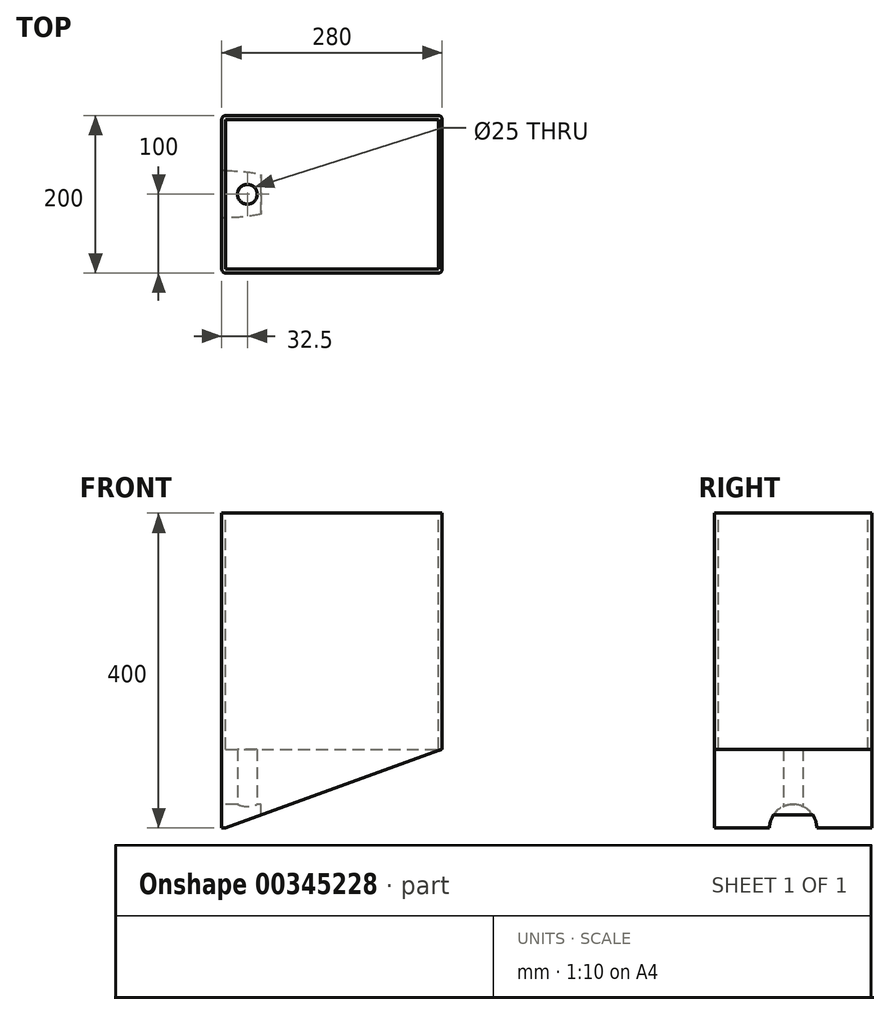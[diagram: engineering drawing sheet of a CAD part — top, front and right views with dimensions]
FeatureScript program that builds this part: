
annotation { "Feature Type Name" : "Feature", "Feature Type Description" : "" }
export const myFeature = defineFeature(function(context is Context, id is Id, definition is map)
    precondition{}
    {
        {
            var Q0;
            Q0=qCreatedBy(makeId("Top.planeOp"),FACE);
            var sketch = newSketch(context, id + "F0", { "sketchPlane" : qUnion([Q0])});
            skLineSegment(sketch, "E0.bottom", {"start": v(-140, 100) * mm, "end": v(140, 100) * mm});
            skLineSegment(sketch, "E0.top", {"start": v(-140, -100) * mm, "end": v(140, -100) * mm});
            skLineSegment(sketch, "E0.left", {"start": v(-140, 100) * mm, "end": v(-140, -100) * mm});
            skLineSegment(sketch, "E0.right", {"start": v(140, 100) * mm, "end": v(140, -100) * mm});
            skPoint(sketch, "E0.middle", {"position": v(0, 0) * mm});
            skCircle(sketch, "E1", {"center": v(-107.5, 0) * mm, "radius": 12.5 * mm});
            skSolve(sketch);
        }
        {
            var Q0;
            Q0=makeQuery(id+"F0.imprint","IMPRINT",FACE,{"disambiguationData":[TD([[makeQuery(id+"F0.imprint","IMPRINT",EDGE,{"derivedFrom":sQuery(id+"F0.wireOp",EDGE,"E0.bottom")}),-1.0]])]});
            extrude(context, id + "F1", {"entities" : qUnion([Q0]), "depth" : 400 * mm});
        }
        {
            var Q0;
            Q0=makeQuery(id+"F1.opExtrude","CAP_FACE",FACE,{"disambiguationData":[OSD([sQuery(id+"F0.wireOp",EDGE,"E0.bottom"),sQuery(id+"F0.wireOp",EDGE,"E0.top"),sQuery(id+"F0.wireOp",EDGE,"E0.left"),sQuery(id+"F0.wireOp",EDGE,"E0.right")])],"isStart":false});
            var sketch = newSketch(context, id + "F2", { "sketchPlane" : qUnion([Q0])});
            skLineSegment(sketch, "E2.bottom", {"start": v(-135, 95) * mm, "end": v(135, 95) * mm});
            skLineSegment(sketch, "E2.top", {"start": v(-135, -95) * mm, "end": v(135, -95) * mm});
            skLineSegment(sketch, "E2.left", {"start": v(-135, 95) * mm, "end": v(-135, -95) * mm});
            skLineSegment(sketch, "E2.right", {"start": v(135, 95) * mm, "end": v(135, -95) * mm});
            skPoint(sketch, "E2.middle", {"position": v(0, 0) * mm});
            skSolve(sketch);
        }
        {
            var Q0;
            Q0=qSketchRegion(id+"F2",true);
            extrude(context, id + "F3", {"entities" : qUnion([Q0]), "operationType" : NewBodyOperationType.REMOVE, "oppositeDirection" : true, "depth" : 300 * mm});
        }
        {
            var Q0;
            Q0=makeQuery(id+"F1.opExtrude","SWEPT_FACE",FACE,{"disambiguationData":[OSD([sQuery(id+"F0.wireOp",EDGE,"E0.left")])]});
            var sketch = newSketch(context, id + "F4", { "sketchPlane" : qUnion([Q0])});
            skPoint(sketch, "E3.middle", {"position": v(0, 29.4) * mm});
            skCircle(sketch, "E4", {"center": v(0, 0) * mm, "radius": 30 * mm});
            skSolve(sketch);
        }
        {
            var Q0;
            Q0=qSketchRegion(id+"F4",true);
            extrude(context, id + "F5", {"entities" : qUnion([Q0]), "operationType" : NewBodyOperationType.REMOVE, "oppositeDirection" : true, "depth" : 50 * mm});
        }
        {
            var Q0;
            Q0=makeQuery(id+"F1.opExtrude","SWEPT_EDGE",EDGE,{"disambiguationData":[OSD([sQuery(id+"F0.wireOp",EDGE,"E0.top"),sQuery(id+"F0.wireOp",EDGE,"E0.left")])]});
            var Q1;
            Q1=makeQuery(id+"F1.opExtrude","SWEPT_EDGE",EDGE,{"disambiguationData":[OSD([sQuery(id+"F0.wireOp",EDGE,"E0.bottom"),sQuery(id+"F0.wireOp",EDGE,"E0.left")])]});
            var Q2;
            Q2=makeQuery(id+"F1.opExtrude","SWEPT_EDGE",EDGE,{"disambiguationData":[OSD([sQuery(id+"F0.wireOp",EDGE,"E0.bottom"),sQuery(id+"F0.wireOp",EDGE,"E0.right")])]});
            var Q3;
            Q3=makeQuery(id+"F1.opExtrude","SWEPT_EDGE",EDGE,{"disambiguationData":[OSD([sQuery(id+"F0.wireOp",EDGE,"E0.top"),sQuery(id+"F0.wireOp",EDGE,"E0.right")])]});
            fillet(context, id + "F6", {"entities" : qUnion([Q0, Q1, Q2, Q3]), "radius" : 5 * mm, "tangentPropagation" : true, "allowEdgeOverflow" : false});
        }
        {
            var Q0;
            Q0=makeQuery(id+"F1.opExtrude","SWEPT_FACE",FACE,{"disambiguationData":[OSD([sQuery(id+"F0.wireOp",EDGE,"E0.top")])]});
            var sketch = newSketch(context, id + "F7", { "sketchPlane" : qUnion([Q0])});
            skLineSegment(sketch, "E5", {"start": v(-135, 0) * mm, "end": v(141.27, 100.55) * mm});
            skLineSegment(sketch, "E6", {"start": v(141.27, 100.55) * mm, "end": v(141.27, 0) * mm});
            skLineSegment(sketch, "E7", {"start": v(141.27, 0) * mm, "end": v(-135, 0) * mm});
            skSolve(sketch);
        }
        {
            var Q0;
            Q0=qSketchRegion(id+"F7",true);
            extrude(context, id + "F8", {"entities" : qUnion([Q0]), "operationType" : NewBodyOperationType.REMOVE, "oppositeDirection" : true, "depth" : 280 * mm});
        }
    });
